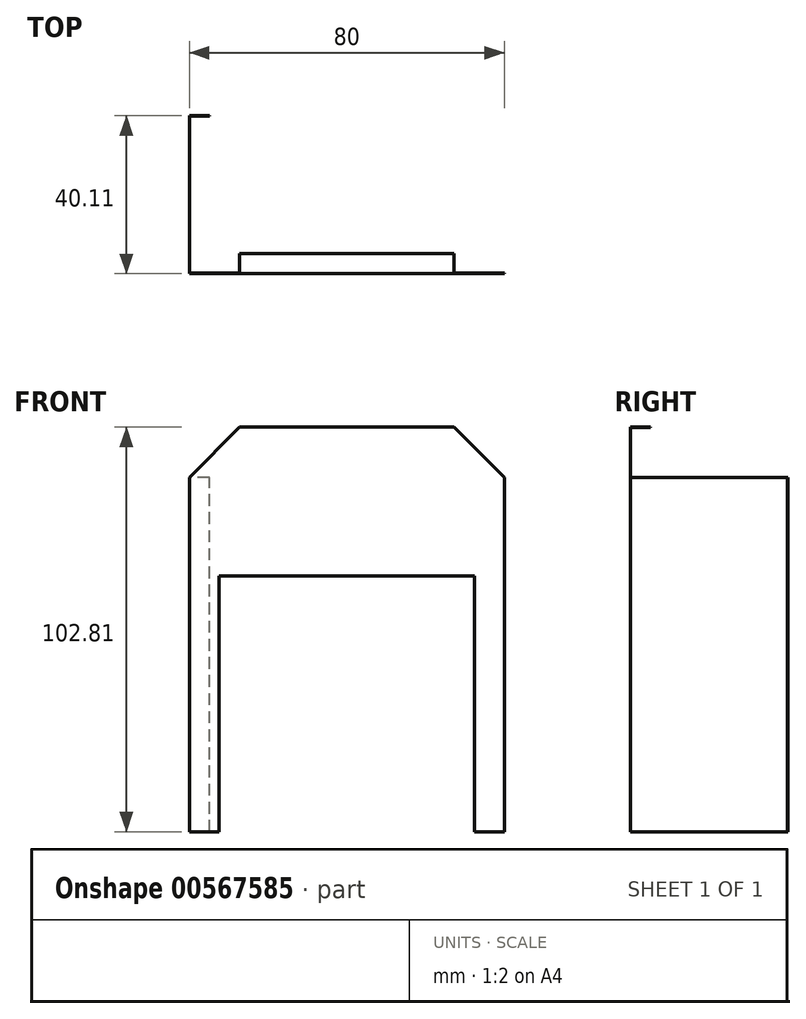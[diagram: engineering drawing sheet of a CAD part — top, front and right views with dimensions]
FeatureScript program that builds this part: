
annotation { "Feature Type Name" : "Feature", "Feature Type Description" : "" }
export const myFeature = defineFeature(function(context is Context, id is Id, definition is map)
    precondition{}
    {
        {
            var Q0;
            Q0=qCreatedBy(makeId("Front.planeOp"),FACE);
            var sketch = newSketch(context, id + "F0", { "sketchPlane" : qUnion([Q0])});
            skLineSegment(sketch, "E0", {"start": v(0, 0) * mm, "end": v(12.8, 12.8) * mm});
            skLineSegment(sketch, "E1", {"start": v(12.8, 12.8) * mm, "end": v(67.2, 12.8) * mm});
            skLineSegment(sketch, "E2", {"start": v(67.2, 12.8) * mm, "end": v(80, 0) * mm});
            skLineSegment(sketch, "E3", {"start": v(80, 0) * mm, "end": v(80, -90) * mm});
            skLineSegment(sketch, "E4", {"start": v(80, -90) * mm, "end": v(72.5, -90) * mm});
            skLineSegment(sketch, "E5", {"start": v(72.5, -90) * mm, "end": v(72.5, -25) * mm});
            skLineSegment(sketch, "E6", {"start": v(72.5, -25) * mm, "end": v(7.5, -25) * mm});
            skLineSegment(sketch, "E7", {"start": v(7.5, -25) * mm, "end": v(7.5, -90) * mm});
            skLineSegment(sketch, "E8", {"start": v(7.5, -90) * mm, "end": v(0, -90) * mm});
            skLineSegment(sketch, "E9", {"start": v(0, -90) * mm, "end": v(0, 0) * mm});
            skSolve(sketch);
        }
        {
            var Q0;
            Q0=makeQuery(id+"F0.imprint","IMPRINT",FACE,{"disambiguationData":[TD([[makeQuery(id+"F0.imprint","IMPRINT",EDGE,{"derivedFrom":sQuery(id+"F0.wireOp",EDGE,"E0")}),-1.0]])]});
            extrude(context, id + "F1", {"entities" : qUnion([Q0]), "depth" : 0.1 * mm, "offsetDistance" : 25 * mm});
        }
        {
            var Q0;
            Q0=makeQuery(id+"F1.opExtrude","CAP_FACE",FACE,{"disambiguationData":[OSD([sQuery(id+"F0.wireOp",EDGE,"E0"),sQuery(id+"F0.wireOp",EDGE,"E1"),sQuery(id+"F0.wireOp",EDGE,"E2"),sQuery(id+"F0.wireOp",EDGE,"E3"),sQuery(id+"F0.wireOp",EDGE,"E4"),sQuery(id+"F0.wireOp",EDGE,"E5"),sQuery(id+"F0.wireOp",EDGE,"E6"),sQuery(id+"F0.wireOp",EDGE,"E7"),sQuery(id+"F0.wireOp",EDGE,"E8"),sQuery(id+"F0.wireOp",EDGE,"E9"),sQuery(id+"F0.wireOp",EDGE,"erwrTCqY-L0vN-HkaI-yH3F-FEG5CYT5yQRY"),sQuery(id+"F0.wireOp",EDGE,"YmA8WcoS-wNMU-x3Wz-45K6-kiu0AFeHS7Pc"),sQuery(id+"F0.wireOp",EDGE,"M1gbDPhO-9vrp-2S9M-ZdJS-tJd0vjTFnCFq"),sQuery(id+"F0.wireOp",EDGE,"kXmvf3Ym-KRzL-WieB-HZAy-8x5OfnpSxJKE"),sQuery(id+"F0.wireOp",EDGE,"bBNtrSCT-cWMW-9hxm-W5TU-fXJUiRUwagEI"),sQuery(id+"F0.wireOp",EDGE,"WXK9EFgR-9xXD-05L6-agt7-xb33hSqukXnF"),sQuery(id+"F0.wireOp",EDGE,"lPt3jZt0-HMhW-elXi-6iLg-KnUtY0EG7iZ9"),sQuery(id+"F0.wireOp",EDGE,"diooy62x-LLFg-7XWc-a9U7-1JwjTS6y2ptn"),sQuery(id+"F0.wireOp",EDGE,"JQFHF39j-eX5A-jZmB-tAmv-BqxlipgMAiAE"),sQuery(id+"F0.wireOp",EDGE,"VqxTl7wK-Decx-K9Sj-99qQ-g00B0AxBlygl")])],"isStart":true});
            var sketch = newSketch(context, id + "F2", { "sketchPlane" : qUnion([Q0])});
            skLineSegment(sketch, "E10", {"start": v(-79.9, -90) * mm, "end": v(-79.9, 0) * mm});
            skLineSegment(sketch, "E11", {"start": v(-79.89, 0) * mm, "end": v(-80, 0) * mm});
            skLineSegment(sketch, "E12", {"start": v(-80, -90) * mm, "end": v(-79.89, -90) * mm});
            skLineSegment(sketch, "E13", {"start": v(0, -90) * mm, "end": v(-0.1, -90) * mm});
            skLineSegment(sketch, "E14", {"start": v(-0.1, -90) * mm, "end": v(-0.1, 0) * mm});
            skLineSegment(sketch, "E15", {"start": v(-0.1, 0) * mm, "end": v(0, 0) * mm});
            skSolve(sketch);
        }
        {
            var Q0;
            Q0=makeQuery(id+"F2.imprint","IMPRINT",FACE,{"disambiguationData":[TD([[makeQuery(id+"F2.imprint","IMPRINT",EDGE,{"derivedFrom":sQuery(id+"F2.wireOp",EDGE,"E13")}),1.0]])]});
            extrude(context, id + "F3", {"entities" : qUnion([Q0]), "operationType" : NewBodyOperationType.ADD, "depth" : 40 * mm, "offsetDistance" : 25 * mm});
        }
        {
            var Q0;
            Q0=makeQuery(id+"F3.opExtrude","SWEPT_FACE",FACE,{"disambiguationData":[OSD([sQuery(id+"F2.wireOp",EDGE,"E14")])]});
            var sketch = newSketch(context, id + "F4", { "sketchPlane" : qUnion([Q0])});
            skLineSegment(sketch, "E16", {"start": v(40, 0) * mm, "end": v(39.89, 0) * mm});
            skLineSegment(sketch, "E17", {"start": v(39.89, 0) * mm, "end": v(39.9, -90) * mm});
            skSolve(sketch);
        }
        {
            var Q0;
            Q0=makeQuery(id+"F4.imprint","IMPRINT",FACE,{"disambiguationData":[TD([[makeQuery(id+"F4.imprint","IMPRINT",EDGE,{"derivedFrom":sQuery(id+"F4.wireOp",EDGE,"E16")}),1.0]])]});
            extrude(context, id + "F5", {"entities" : qUnion([Q0]), "operationType" : NewBodyOperationType.ADD, "depth" : 5 * mm, "offsetDistance" : 25 * mm});
        }
        {
            var Q0;
            Q0=makeQuery(id+"F0.imprint","IMPRINT",FACE,{"disambiguationData":[TD([[makeQuery(id+"F0.imprint","IMPRINT",EDGE,{"derivedFrom":sQuery(id+"F0.wireOp",EDGE,"E0")}),-1.0]])]});
            var sketch = newSketch(context, id + "F6", { "sketchPlane" : qUnion([Q0])});
            skLineSegment(sketch, "E18.0", {"start": v(12.8, 12.7) * mm, "end": v(67.2, 12.7) * mm});
            skLineSegment(sketch, "E19", {"start": v(67.2, 12.7) * mm, "end": v(67.2, 12.8) * mm});
            skLineSegment(sketch, "E20", {"start": v(12.8, 12.7) * mm, "end": v(12.8, 12.8) * mm});
            skLineSegment(sketch, "E21", {"start": v(67.2, 12.8) * mm, "end": v(12.8, 12.8) * mm});
            skSolve(sketch);
        }
        {
            var Q0;
            Q0 = qSketchRegion(id + "F6", true);
            extrude(context, id + "F7", {"entities" : qUnion([Q0]), "operationType" : NewBodyOperationType.ADD, "oppositeDirection" : true, "depth" : 5 * mm, "offsetDistance" : 25 * mm});
        }
    });
